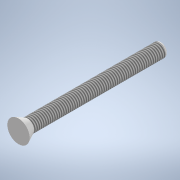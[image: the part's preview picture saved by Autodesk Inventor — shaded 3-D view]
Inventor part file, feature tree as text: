
AUTODESK INVENTOR PART (.ipt)
format: ipt  version: 2020 (Build 240168000, 168)  size: 114,176 bytes
history: native  units: mm
features: revolve x1, fillet x1, thread x1, sketch x1
ambient origin geometry x8: Origin, YZ Plane, XZ Plane, XY Plane, X Axis, Y Axis, Z Axis, Center Point
bodies: Solido1 (feature_tree)
feature tree (4):
  revolve  "Rivoluzione1"
  fillet  "Raccordo1"  Radius=1.5mm
  thread  "Filettatura1"
  sketch  "Schizzo1"
